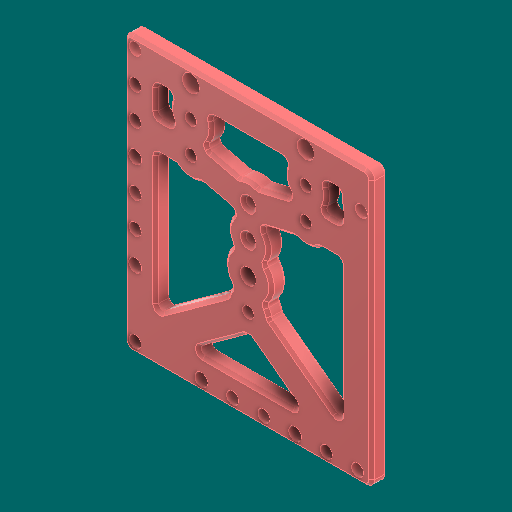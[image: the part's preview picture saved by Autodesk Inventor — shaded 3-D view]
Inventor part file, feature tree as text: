
AUTODESK INVENTOR PART (.ipt)
format: ipt  version: 2023.1 (Build 271208000, 208)  size: 577,536 bytes
history: native  units: in
note: dims shown in document units (in); Inventor stores cm internally (conversion verified against a paired STEP export)
features: other x3, sketch x2
ambient origin geometry x8: Origin, YZ Plane, XZ Plane, XY Plane, X Axis, Y Axis, Z Axis, Center Point
bodies: Solid1 (feature_tree)
feature tree (5):
  other  "TopPlate_MIR.ipt"
  other  "Solid1::TopPlate_MIR.ipt"
  other  "TaggingFeature1"
  sketch  "Sketch1"  dims[d0=0.3937in]
  sketch  "Sketch2"
